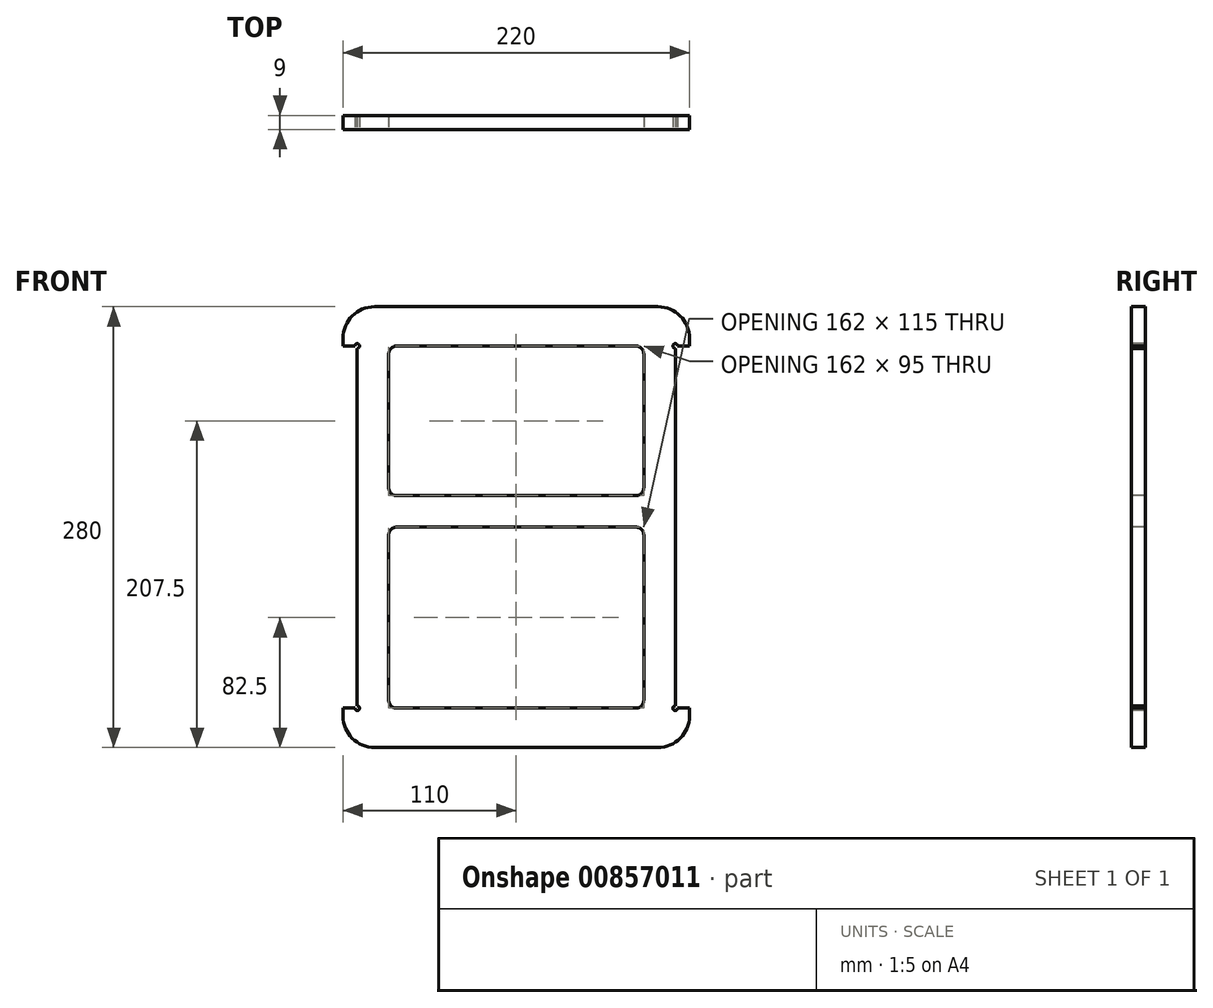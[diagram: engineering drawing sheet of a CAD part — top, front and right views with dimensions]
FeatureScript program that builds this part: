
annotation { "Feature Type Name" : "Feature", "Feature Type Description" : "" }
export const myFeature = defineFeature(function(context is Context, id is Id, definition is map)
    precondition{}
    {
        {
            var Q0;
            Q0=qCreatedBy(makeId("Front.planeOp"),FACE);
            var sketch = newSketch(context, id + "F0", { "sketchPlane" : qUnion([Q0])});
            skLineSegment(sketch, "E0.bottom", {"start": v(-90, 140) * mm, "end": v(90, 140) * mm});
            skLineSegment(sketch, "E0.top", {"start": v(-90, -140) * mm, "end": v(90, -140) * mm});
            skLineSegment(sketch, "E0.left", {"start": v(-110, 120) * mm, "end": v(-110, 115) * mm});
            skLineSegment(sketch, "E0.right", {"start": v(110, 120) * mm, "end": v(110, 115) * mm});
            skPoint(sketch, "E0.middle", {"position": v(0, 0) * mm});
            skLineSegment(sketch, "E1.bottom", {"start": v(-76, 20) * mm, "end": v(76, 20) * mm});
            skLineSegment(sketch, "E2", {"start": v(-110, 115) * mm, "end": v(-101, 115) * mm});
            skLineSegment(sketch, "E3", {"start": v(-110, -115) * mm, "end": v(-101, -115) * mm});
            skLineSegment(sketch, "E4.0", {"start": v(-101, 115) * mm, "end": v(-101, -115) * mm});
            skLineSegment(sketch, "E5.trimOffspring", {"start": v(-110, -115) * mm, "end": v(-110, -120) * mm});
            skLineSegment(sketch, "E6.0", {"start": v(-81, 110) * mm, "end": v(-81, 25) * mm});
            skLineSegment(sketch, "E7.0", {"start": v(81, 110) * mm, "end": v(81, 25) * mm});
            skLineSegment(sketch, "E8.trimOffspring", {"start": v(-76, 115) * mm, "end": v(76, 115) * mm});
            skLineSegment(sketch, "E9.trimOffspring", {"start": v(-81, -5) * mm, "end": v(-81, -110) * mm});
            skLineSegment(sketch, "E10.trimOffspring", {"start": v(-76, -115) * mm, "end": v(76, -115) * mm});
            skLineSegment(sketch, "E11.trimOffspring", {"start": v(-76, 0) * mm, "end": v(76, 0) * mm});
            skPoint(sketch, "E12.visualSharp", {"position": v(-110, 140) * mm});
            skArc(sketch, "E12.filletArc", {"start": v(-90, 140) * mm, "mid": v(-104.14, 134.14) * mm, "end": v(-110, 120) * mm});
            skPoint(sketch, "E13.visualSharp", {"position": v(110, 140) * mm});
            skArc(sketch, "E13.filletArc", {"start": v(110, 120) * mm, "mid": v(104.14, 134.14) * mm, "end": v(90, 140) * mm});
            skPoint(sketch, "E14.visualSharp", {"position": v(110, -140) * mm});
            skArc(sketch, "E14.filletArc", {"start": v(90, -140) * mm, "mid": v(104.14, -134.14) * mm, "end": v(110, -120) * mm});
            skPoint(sketch, "E15.visualSharp", {"position": v(-110, -140) * mm});
            skArc(sketch, "E15.filletArc", {"start": v(-110, -120) * mm, "mid": v(-104.14, -134.14) * mm, "end": v(-90, -140) * mm});
            skLineSegment(sketch, "E16.trimOffspring", {"start": v(110, -115) * mm, "end": v(110, -120) * mm});
            skLineSegment(sketch, "E17.trimOffspring", {"start": v(101, -115) * mm, "end": v(110, -115) * mm});
            skLineSegment(sketch, "E18.trimOffspring", {"start": v(81, -5) * mm, "end": v(81, -110) * mm});
            skLineSegment(sketch, "E19.trimOffspring", {"start": v(101, 115) * mm, "end": v(101, -115) * mm});
            skLineSegment(sketch, "E20.trimOffspring", {"start": v(101, 115) * mm, "end": v(110, 115) * mm});
            skPoint(sketch, "E21.visualSharp", {"position": v(81, 20) * mm});
            skArc(sketch, "E21.filletArc", {"start": v(76, 20) * mm, "mid": v(79.54, 21.46) * mm, "end": v(81, 25) * mm});
            skPoint(sketch, "E22.visualSharp", {"position": v(-81, 20) * mm});
            skArc(sketch, "E22.filletArc", {"start": v(-81, 25) * mm, "mid": v(-79.54, 21.46) * mm, "end": v(-76, 20) * mm});
            skPoint(sketch, "E23.visualSharp", {"position": v(-81, 0) * mm});
            skArc(sketch, "E23.filletArc", {"start": v(-76, 0) * mm, "mid": v(-79.54, -1.46) * mm, "end": v(-81, -5) * mm});
            skPoint(sketch, "E24.visualSharp", {"position": v(81, 0) * mm});
            skArc(sketch, "E24.filletArc", {"start": v(81, -5) * mm, "mid": v(79.54, -1.46) * mm, "end": v(76, 0) * mm});
            skPoint(sketch, "E25.visualSharp", {"position": v(81, -115) * mm});
            skArc(sketch, "E25.filletArc", {"start": v(76, -115) * mm, "mid": v(79.54, -113.54) * mm, "end": v(81, -110) * mm});
            skPoint(sketch, "E26.visualSharp", {"position": v(-81, -115) * mm});
            skArc(sketch, "E26.filletArc", {"start": v(-81, -110) * mm, "mid": v(-79.54, -113.54) * mm, "end": v(-76, -115) * mm});
            skPoint(sketch, "E27.visualSharp", {"position": v(-81, 115) * mm});
            skArc(sketch, "E27.filletArc", {"start": v(-76, 115) * mm, "mid": v(-79.54, 113.54) * mm, "end": v(-81, 110) * mm});
            skPoint(sketch, "E28.visualSharp", {"position": v(81, 115) * mm});
            skArc(sketch, "E28.filletArc", {"start": v(81, 110) * mm, "mid": v(79.54, 113.54) * mm, "end": v(76, 115) * mm});
            skCircle(sketch, "E29", {"center": v(-101, 115) * mm, "radius": 1.5 * mm});
            skCircle(sketch, "E30", {"center": v(101, 115) * mm, "radius": 1.5 * mm});
            skCircle(sketch, "E31", {"center": v(-101, -115) * mm, "radius": 1.5 * mm});
            skCircle(sketch, "E32", {"center": v(101, -115) * mm, "radius": 1.5 * mm});
            skSolve(sketch);
        }
        {
            var Q0;
            Q0=makeQuery(id+"F0.imprint","IMPRINT",FACE,{"disambiguationData":[TD([[makeQuery(id+"F0.imprint","IMPRINT",EDGE,{"derivedFrom":sQuery(id+"F0.wireOp",EDGE,"E0.bottom")}),-1.0]])]});
            extrude(context, id + "F1", {"entities" : qUnion([Q0]), "oppositeDirection" : true, "depth" : 9 * mm, "offsetDistance" : 25 * mm});
        }
    });
